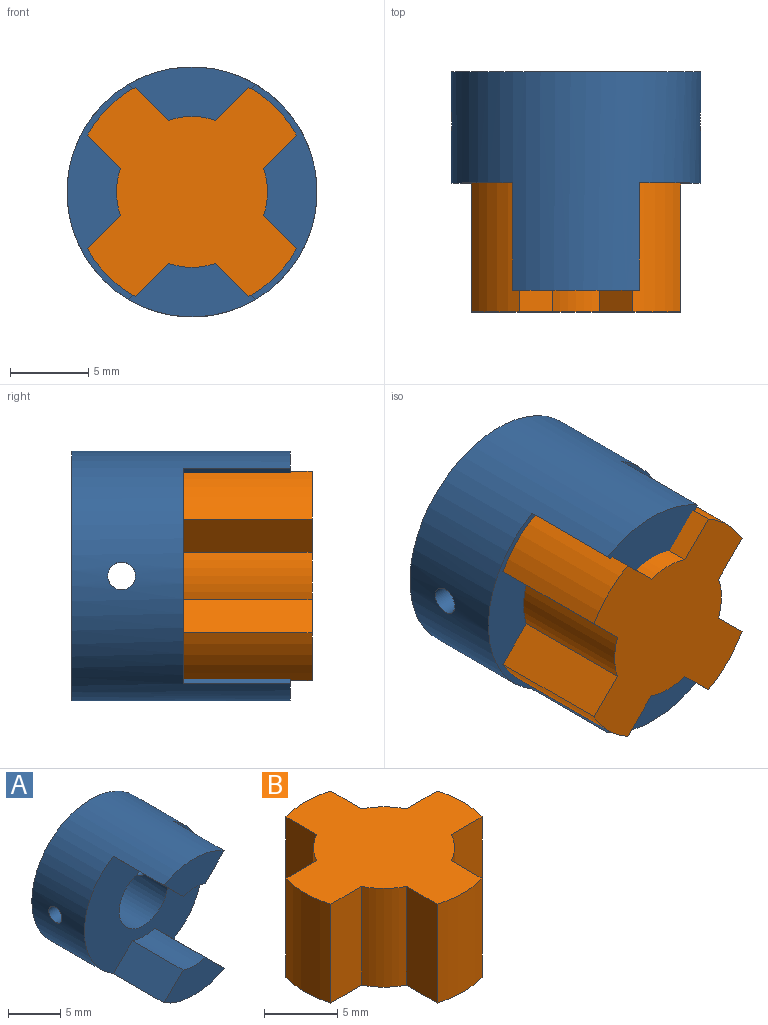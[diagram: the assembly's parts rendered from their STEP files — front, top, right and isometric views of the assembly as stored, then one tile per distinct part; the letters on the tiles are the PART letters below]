
ASSEMBLY  parts=2 mates=1
PART A: 14 faces, bbox 16x14x16 mm
  f0: cylinder r=3.28mm len=7.11mm, axis (0,1,0), area 141.4mm2, adj f4,f11,f12,f13
  f1: cylinder r=8mm len=16mm, axis (0,1,0), area 469.5mm2, adj f2,f3,f4,f5,f6,f8,f9,f11
  f2: plane 8.13x3.68mm, normal (0,-1,0), area 19.9mm2, adj f1,f6,f7,f8
  f3: plane 8.13x3.68mm, normal (0,-1,0), area 19.9mm2, adj f1,f5,f9,f10
  f4: plane 16x16mm, normal (0,1,0), area 167.4mm2, adj f0,f1
  f5: plane 6.86x2.57mm, normal (-0.71,0,-0.71), area 24.9mm2, adj f1,f3,f10,f11
  f6: plane 6.86x2.57mm, normal (-0.71,0,0.71), area 24.9mm2, adj f1,f2,f7,f11
  f7: cylinder r=4.57mm len=6.86mm, axis (0,-1,0), area 20.9mm2, adj f2,f6,f8,f11
  f8: plane 6.86x2.57mm, normal (0.71,0,0.71), area 24.9mm2, adj f1,f2,f7,f11
  f9: plane 6.86x2.57mm, normal (0.71,0,-0.71), area 24.9mm2, adj f1,f3,f10,f11
  f10: cylinder r=4.57mm len=6.86mm, axis (0,-1,0), area 20.9mm2, adj f3,f5,f9,f11
  f11: plane 16x13.78mm, normal (0,-1,0), area 127.6mm2, adj f0,f1,f5,f6,f7,f8,f9,f10
  f12: cylinder r=0.89mm len=4.85mm, axis (1,0,0), area 26.6mm2, adj f0,f1
  f13: cylinder r=0.89mm len=4.85mm, axis (1,0,0), area 26.6mm2, adj f0,f1
PART B: 18 faces, bbox 15.2x15.2x8.3 mm
  f0: cylinder r=7.62mm len=8.26mm, axis (0,0,-1), area 36.1mm2, adj f3,f4,f14,f17
  f1: cylinder r=7.62mm len=8.26mm, axis (0,0,-1), area 36.1mm2, adj f3,f4,f11,f12
  f2: cylinder r=7.62mm len=8.26mm, axis (0,0,-1), area 36.1mm2, adj f3,f4,f6,f9
  f3: plane 15.24x15.24mm, normal (0,0,1), area 122.5mm2, adj f0,f1,f2,f5,f6,f7,f8,f9
  f4: plane 15.24x15.24mm, normal (0,0,-1), area 122.5mm2, adj f0,f1,f2,f5,f6,f7,f8,f9
  f5: cylinder r=7.62mm len=8.26mm, axis (0,0,-1), area 36.1mm2, adj f3,f4,f7,f16
  f6: plane 8.26x2.99mm, normal (-1,0,0), area 24.7mm2, adj f2,f3,f4,f8
  f7: plane 8.26x2.99mm, normal (0,1,0), area 24.7mm2, adj f3,f4,f5,f8
  f8: cylinder r=4.83mm len=8.26mm, axis (0,0,1), area 25.6mm2, adj f3,f4,f6,f7
  f9: plane 8.26x2.99mm, normal (1,0,0), area 24.7mm2, adj f2,f3,f4,f10
  f10: cylinder r=4.83mm len=8.26mm, axis (0,0,1), area 25.6mm2, adj f3,f4,f9,f11
  f11: plane 8.26x2.99mm, normal (0,1,0), area 24.7mm2, adj f1,f3,f4,f10
  f12: plane 8.26x2.99mm, normal (0,-1,0), area 24.7mm2, adj f1,f3,f4,f13
  f13: cylinder r=4.83mm len=8.26mm, axis (0,0,1), area 25.6mm2, adj f3,f4,f12,f14
  f14: plane 8.26x2.99mm, normal (1,0,0), area 24.7mm2, adj f0,f3,f4,f13
  f15: cylinder r=4.83mm len=8.26mm, axis (0,0,1), area 25.6mm2, adj f3,f4,f16,f17
  f16: plane 8.26x2.99mm, normal (0,-1,0), area 24.7mm2, adj f3,f4,f5,f15
  f17: plane 8.26x2.99mm, normal (-1,0,0), area 24.7mm2, adj f0,f3,f4,f15
PLACE A at identity fixed
PLACE B rot(axis=(-0.28,-0.68,-0.68),148.6deg) t=(0,-4.25,0)mm
MATE fastened B.f0 <-> A.f0  axis (0,1,0) through (0,-0.13,0)mm
